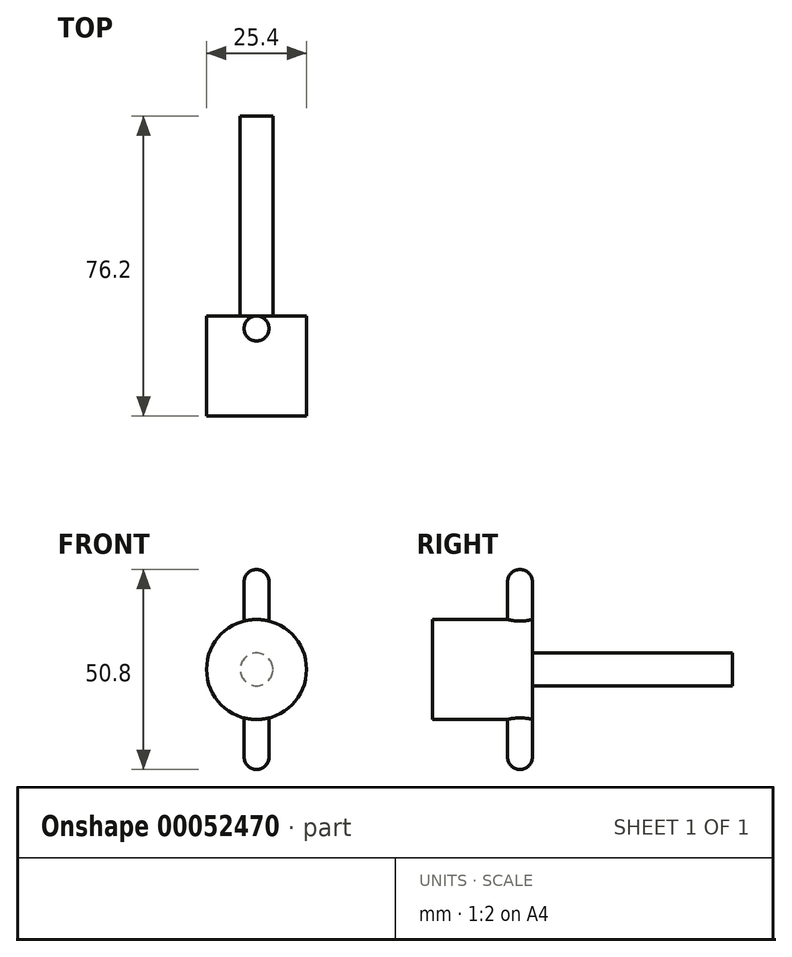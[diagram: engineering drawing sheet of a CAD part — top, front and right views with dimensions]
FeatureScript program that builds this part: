
annotation { "Feature Type Name" : "Feature", "Feature Type Description" : "" }
export const myFeature = defineFeature(function(context is Context, id is Id, definition is map)
    precondition{}
    {
        {
            var Q0;
            Q0=qCreatedBy(makeId("Front.planeOp"),FACE);
            var sketch = newSketch(context, id + "F0", { "sketchPlane" : qUnion([Q0])});
            skCircle(sketch, "E0", {"center": v(0, 0) * mm, "radius": 12.7 * mm});
            skSolve(sketch);
        }
        {
            var Q0;
            Q0=qSketchRegion(id+"F0",true);
            extrude(context, id + "F1", {"entities" : qUnion([Q0]), "depth" : 25.4 * mm});
        }
        {
            var Q0;
            Q0=qCreatedBy(makeId("Top.planeOp"),FACE);
            var sketch = newSketch(context, id + "F2", { "sketchPlane" : qUnion([Q0])});
            skCircle(sketch, "E1", {"center": v(0, -3.18) * mm, "radius": 3.18 * mm});
            skSolve(sketch);
        }
        {
            var Q0;
            Q0=qSketchRegion(id+"F2",true);
            extrude(context, id + "F3", {"entities" : qUnion([Q0]), "operationType" : NewBodyOperationType.ADD, "endBound" : BoundingType.SYMMETRIC, "depth" : 50.8 * mm});
        }
        {
            var Q0;
            Q0=makeQuery(id+"F3.opExtrude","CAP_EDGE",EDGE,{"disambiguationData":[OSD([sQuery(id+"F2.wireOp",EDGE,"E1")])],"isStart":true});
            var Q1;
            Q1=makeQuery(id+"F3.opExtrude","CAP_EDGE",EDGE,{"disambiguationData":[OSD([sQuery(id+"F2.wireOp",EDGE,"E1")])],"isStart":false});
            fillet(context, id + "F4", {"entities" : qUnion([Q0, Q1]), "radius" : 3.17 * mm, "tangentPropagation" : true, "allowEdgeOverflow" : false});
        }
        {
            var Q0;
            Q0=makeQuery(id+"F1.opExtrude","CAP_FACE",FACE,{"disambiguationData":[OSD([sQuery(id+"F0.wireOp",EDGE,"E0")])],"isStart":true});
            var sketch = newSketch(context, id + "F5", { "sketchPlane" : qUnion([Q0])});
            skCircle(sketch, "E2", {"center": v(0, 0) * mm, "radius": 4.18 * mm});
            skSolve(sketch);
        }
        {
            var Q0;
            Q0 = qSketchRegion(id + "F5", true);
            extrude(context, id + "F6", {"entities" : qUnion([Q0]), "depth" : 50.8 * mm});
        }
    });
